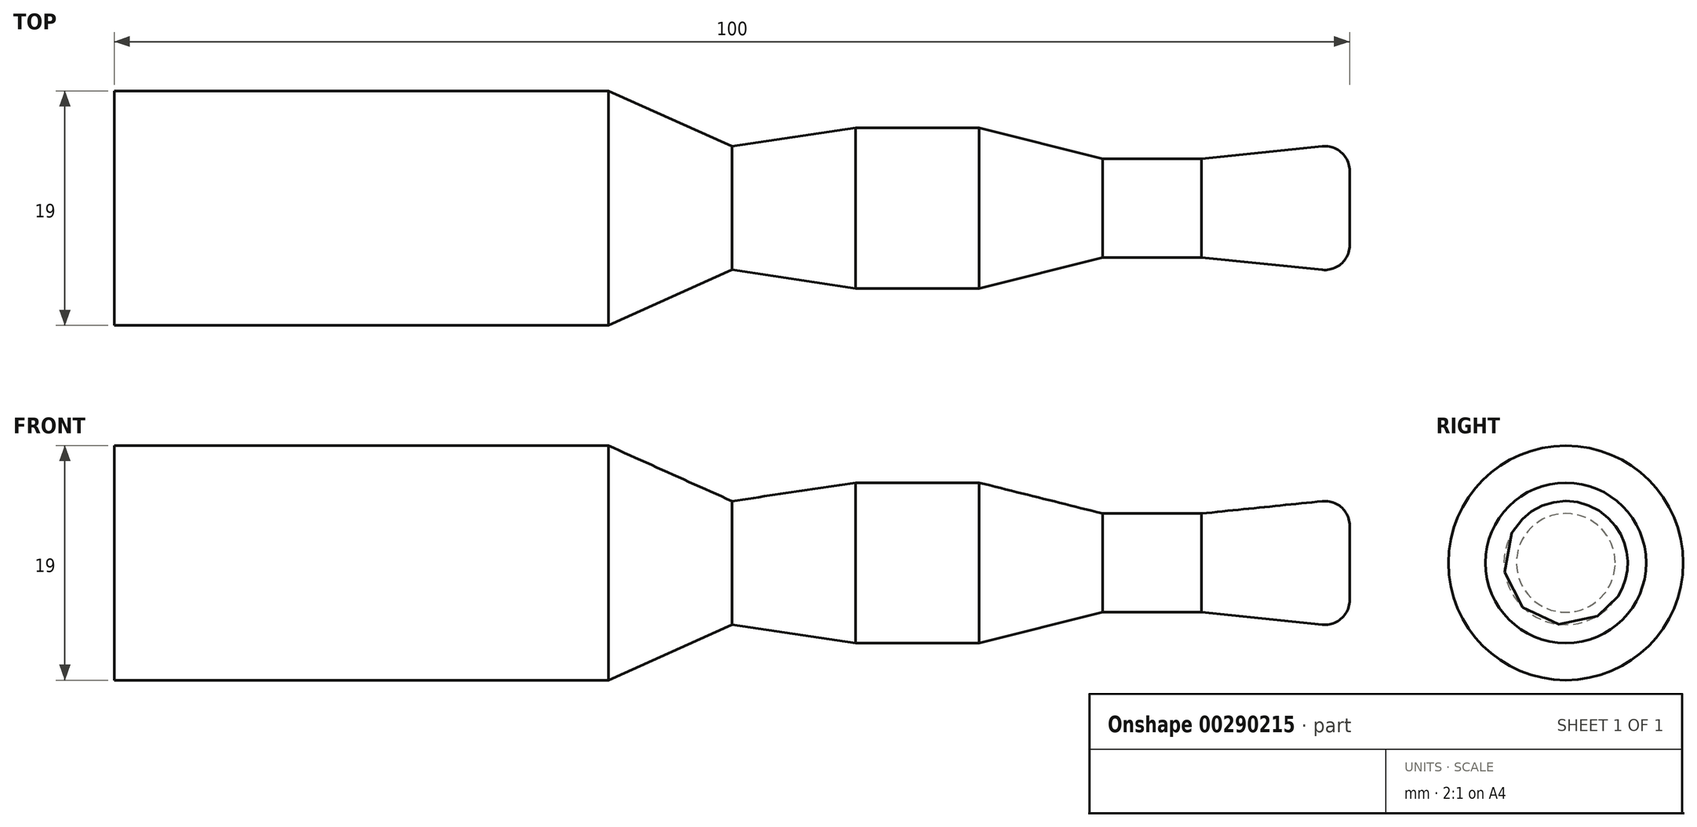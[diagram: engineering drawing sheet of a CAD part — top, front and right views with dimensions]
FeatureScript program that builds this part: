
annotation { "Feature Type Name" : "Feature", "Feature Type Description" : "" }
export const myFeature = defineFeature(function(context is Context, id is Id, definition is map)
    precondition{}
    {
        {
            var Q0;
            Q0=qCreatedBy(makeId("Front.planeOp"),FACE);
            var sketch = newSketch(context, id + "F0", { "sketchPlane" : qUnion([Q0])});
            skLineSegment(sketch, "E0", {"start": v(0, 0) * mm, "end": v(0, 3.01) * mm});
            skArc(sketch, "E1", {"start": v(0, 3.01) * mm, "mid": v(-0.66, 4.5) * mm, "end": v(-2.2, 5) * mm});
            skLineSegment(sketch, "E2", {"start": v(-2.2, 5) * mm, "end": v(-12, 4) * mm});
            skLineSegment(sketch, "E3", {"start": v(-20, 4) * mm, "end": v(-30, 6.5) * mm});
            skLineSegment(sketch, "E4", {"start": v(-30, 6.5) * mm, "end": v(-40, 6.5) * mm});
            skLineSegment(sketch, "E5", {"start": v(-40, 6.5) * mm, "end": v(-50, 5) * mm});
            skLineSegment(sketch, "E6", {"start": v(-50, 5) * mm, "end": v(-60, 9.5) * mm});
            skLineSegment(sketch, "E7", {"start": v(-60, 9.5) * mm, "end": v(-100, 9.5) * mm});
            skLineSegment(sketch, "E8", {"start": v(-100, 9.5) * mm, "end": v(-100, 0) * mm});
            skLineSegment(sketch, "E9", {"start": v(-100, 0) * mm, "end": v(0, 0) * mm});
            skLineSegment(sketch, "E10", {"start": v(-20, 4) * mm, "end": v(-12, 4) * mm});
            skSolve(sketch);
        }
        {
            var Q0;
            Q0=makeQuery(id+"F0.imprint","IMPRINT",FACE,{"disambiguationData":[TD([[makeQuery(id+"F0.imprint","IMPRINT",EDGE,{"derivedFrom":sQuery(id+"F0.wireOp",EDGE,"E0")}),1.0]])]});
            var Q1;
            Q1=sQuery(id+"F0.wireOp",EDGE,"E9");
            revolve(context, id + "F1", {"entities" : qUnion([Q0]), "axis" : qUnion([Q1]), "revolveType" : RevolveType.FULL});
        }
    });
